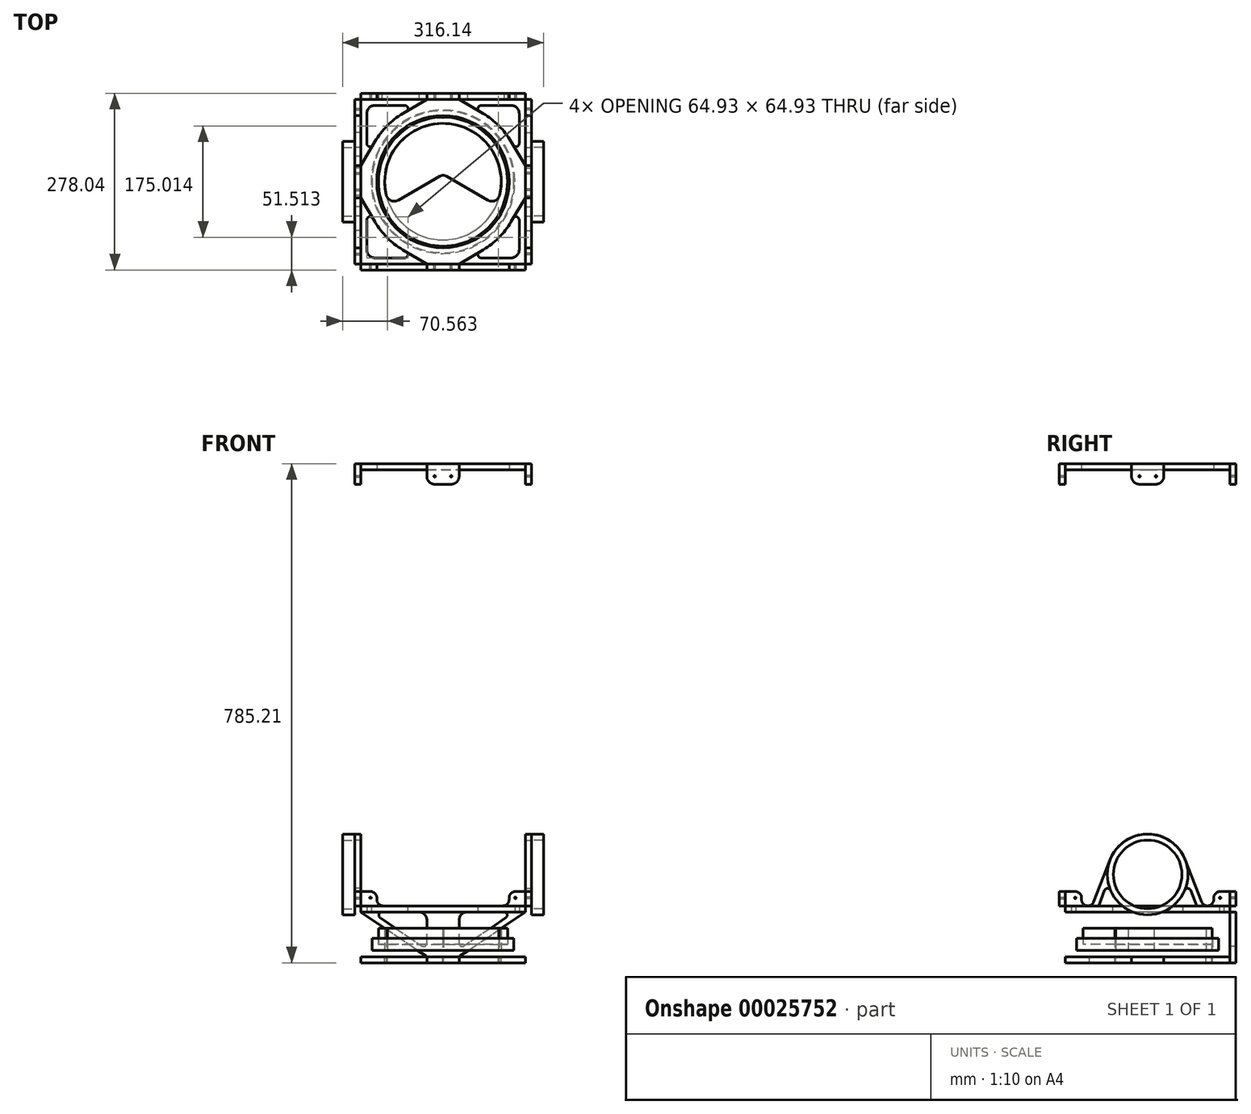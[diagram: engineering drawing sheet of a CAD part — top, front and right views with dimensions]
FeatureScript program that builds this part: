
annotation { "Feature Type Name" : "Feature", "Feature Type Description" : "" }
export const myFeature = defineFeature(function(context is Context, id is Id, definition is map)
    precondition{}
    {
        {
            var Q0;
            Q0=qCreatedBy(makeId("Top.planeOp"),FACE);
            var sketch = newSketch(context, id + "F0", { "sketchPlane" : qUnion([Q0])});
            skCircle(sketch, "E0", {"center": v(0, 0) * mm, "radius": 101.6 * mm});
            skCircle(sketch, "E1", {"center": v(0, 0) * mm, "radius": 101.7 * mm});
            skCircle(sketch, "E2", {"center": v(0, 0) * mm, "radius": 111.7 * mm});
            skCircle(sketch, "E3", {"center": v(0, 0) * mm, "radius": 91.7 * mm});
            skCircle(sketch, "E4", {"center": v(0, 0) * mm, "radius": 10 * mm});
            skLineSegment(sketch, "E5", {"start": v(-10, 0) * mm, "end": v(-10, 91.15) * mm});
            skLineSegment(sketch, "E6", {"start": v(10, 0) * mm, "end": v(10, 91.15) * mm});
            skLineSegment(sketch, "E7", {"start": v(-5, -8.66) * mm, "end": v(73.94, -54.24) * mm});
            skLineSegment(sketch, "E8", {"start": v(5, -8.66) * mm, "end": v(-73.94, -54.24) * mm});
            skLineSegment(sketch, "E9", {"start": v(-5, 8.66) * mm, "end": v(-83.94, -36.92) * mm});
            skLineSegment(sketch, "E10", {"start": v(5, 8.66) * mm, "end": v(83.94, -36.92) * mm});
            skSolve(sketch);
        }
        {
            var Q0;
            Q0=makeQuery(id+"F0.imprint","IMPRINT",FACE,{"disambiguationData":[TD([[makeQuery(id+"F0.imprint","IMPRINT",EDGE,{"derivedFrom":sQuery(id+"F0.wireOp",EDGE,"E0")}),1.0]])]});
            var Q1;
            {var subQ1=sQuery(id+"F0.wireOp",EDGE,"E5");var subQ3=sQuery(id+"F0.wireOp",EDGE,"E3");var subQ5=makeQuery(id+"F0.imprint","INTERSECT",VERTEX,{"derivedFrom":[subQ3,subQ1]});Q1=makeQuery(id+"F0.imprint","IMPRINT",FACE,{"disambiguationData":[TD([[makeQuery(id+"F0.imprint","IMPRINT",EDGE,{"disambiguationData":[TD([[subQ5,-1.0]])],"derivedFrom":subQ3}),1.0]])]});}
            var Q2;
            {var subQ1=sQuery(id+"F0.wireOp",EDGE,"E7");var subQ3=sQuery(id+"F0.wireOp",EDGE,"E3");var subQ5=makeQuery(id+"F0.imprint","INTERSECT",VERTEX,{"derivedFrom":[subQ3,subQ1]});Q2=makeQuery(id+"F0.imprint","IMPRINT",FACE,{"disambiguationData":[TD([[makeQuery(id+"F0.imprint","IMPRINT",EDGE,{"disambiguationData":[TD([[subQ5,1.0]])],"derivedFrom":subQ3}),1.0]])]});}
            var Q3;
            {var subQ3=sQuery(id+"F0.wireOp",EDGE,"E3");var subQ5=sQuery(id+"F0.wireOp",EDGE,"E8");var subQ8=makeQuery(id+"F0.imprint","INTERSECT",VERTEX,{"derivedFrom":[subQ3,subQ5]});Q3=makeQuery(id+"F0.imprint","IMPRINT",FACE,{"disambiguationData":[TD([[makeQuery(id+"F0.imprint","IMPRINT",EDGE,{"disambiguationData":[TD([[subQ8,1.0]])],"derivedFrom":subQ3}),1.0]])]});}
            var Q4;
            {var subQ0=sQuery(id+"F0.wireOp",EDGE,"E4");var subQ2=makeQuery(id+"F0.imprint","INTERSECT",VERTEX,{"derivedFrom":[subQ0,sQuery(id+"F0.wireOp",EDGE,"E6")]});Q4=makeQuery(id+"F0.imprint","IMPRINT",FACE,{"disambiguationData":[TD([[makeQuery(id+"F0.imprint","IMPRINT",EDGE,{"disambiguationData":[TD([[subQ2,-1.0]])],"derivedFrom":subQ0}),1.0]])]});}
            var Q5;
            {var subQ1=sQuery(id+"F0.wireOp",EDGE,"E5");var subQ3=sQuery(id+"F0.wireOp",EDGE,"E4");var subQ5=makeQuery(id+"F0.imprint","INTERSECT",VERTEX,{"derivedFrom":[subQ3,subQ1]});Q5=makeQuery(id+"F0.imprint","IMPRINT",FACE,{"disambiguationData":[TD([[makeQuery(id+"F0.imprint","IMPRINT",EDGE,{"disambiguationData":[TD([[subQ5,1.0]])],"derivedFrom":subQ3}),-1.0]])]});}
            var Q6;
            {var subQ0=sQuery(id+"F0.wireOp",EDGE,"E6");var subQ3=sQuery(id+"F0.wireOp",EDGE,"E4");var subQ4=makeQuery(id+"F0.imprint","INTERSECT",VERTEX,{"derivedFrom":[subQ3,subQ0]});Q6=makeQuery(id+"F0.imprint","IMPRINT",FACE,{"disambiguationData":[TD([[makeQuery(id+"F0.imprint","IMPRINT",EDGE,{"disambiguationData":[TD([[subQ4,-1.0]])],"derivedFrom":subQ3}),-1.0]])]});}
            var Q7;
            {var subQ1=sQuery(id+"F0.wireOp",EDGE,"E7");var subQ3=sQuery(id+"F0.wireOp",EDGE,"E4");var subQ5=makeQuery(id+"F0.imprint","INTERSECT",VERTEX,{"derivedFrom":[subQ3,subQ1]});Q7=makeQuery(id+"F0.imprint","IMPRINT",FACE,{"disambiguationData":[TD([[makeQuery(id+"F0.imprint","IMPRINT",EDGE,{"disambiguationData":[TD([[subQ5,-1.0]])],"derivedFrom":subQ3}),-1.0]])]});}
            var Q8;
            {var subQ3=sQuery(id+"F0.wireOp",EDGE,"E3");var subQ6=sQuery(id+"F0.wireOp",EDGE,"E7");var subQ10=makeQuery(id+"F0.imprint","INTERSECT",VERTEX,{"derivedFrom":[subQ3,subQ6]});Q8=makeQuery(id+"F0.imprint","IMPRINT",FACE,{"disambiguationData":[TD([[makeQuery(id+"F0.imprint","IMPRINT",EDGE,{"disambiguationData":[TD([[subQ10,-1.0]])],"derivedFrom":subQ3}),1.0]])]});}
            var Q9;
            {var subQ0=sQuery(id+"F0.wireOp",EDGE,"E6");var subQ3=sQuery(id+"F0.wireOp",EDGE,"E3");var subQ4=makeQuery(id+"F0.imprint","INTERSECT",VERTEX,{"derivedFrom":[subQ3,subQ0]});Q9=makeQuery(id+"F0.imprint","IMPRINT",FACE,{"disambiguationData":[TD([[makeQuery(id+"F0.imprint","IMPRINT",EDGE,{"disambiguationData":[TD([[subQ4,1.0]])],"derivedFrom":subQ3}),1.0]])]});}
            var Q10;
            {var subQ1=sQuery(id+"F0.wireOp",EDGE,"E5");var subQ5=sQuery(id+"F0.wireOp",EDGE,"E3");var subQ6=makeQuery(id+"F0.imprint","INTERSECT",VERTEX,{"derivedFrom":[subQ5,subQ1]});Q10=makeQuery(id+"F0.imprint","IMPRINT",FACE,{"disambiguationData":[TD([[makeQuery(id+"F0.imprint","IMPRINT",EDGE,{"disambiguationData":[TD([[subQ6,1.0]])],"derivedFrom":subQ5}),1.0]])]});}
            extrude(context, id + "F1", {"entities" : qUnion([Q0, Q1, Q2, Q3, Q4, Q5, Q6, Q7, Q8, Q9, Q10]), "depth" : 25.4 * mm});
        }
        {
            var Q0;
            Q0=makeQuery(id+"F0.imprint","IMPRINT",FACE,{"disambiguationData":[TD([[makeQuery(id+"F0.imprint","IMPRINT",EDGE,{"derivedFrom":sQuery(id+"F0.wireOp",EDGE,"E1")}),-1.0]])]});
            extrude(context, id + "F2", {"entities" : qUnion([Q0]), "depth" : 9.52 * mm});
        }
        {
            var Q0;
            Q0=makeQuery(id+"F0.imprint","IMPRINT",FACE,{"disambiguationData":[TD([[makeQuery(id+"F0.imprint","IMPRINT",EDGE,{"derivedFrom":sQuery(id+"F0.wireOp",EDGE,"E1")}),-1.0]])]});
            var Q1;
            Q1=makeQuery(id+"F0.imprint","IMPRINT",FACE,{"disambiguationData":[TD([[makeQuery(id+"F0.imprint","IMPRINT",EDGE,{"derivedFrom":sQuery(id+"F0.wireOp",EDGE,"E0")}),-1.0]])]});
            var Q2;
            Q2=makeQuery(id+"F0.imprint","IMPRINT",FACE,{"disambiguationData":[TD([[makeQuery(id+"F0.imprint","IMPRINT",EDGE,{"derivedFrom":sQuery(id+"F0.wireOp",EDGE,"E0")}),1.0]])]});
            var Q3;
            {var subQ3=sQuery(id+"F0.wireOp",EDGE,"E3");var subQ6=sQuery(id+"F0.wireOp",EDGE,"E7");var subQ10=makeQuery(id+"F0.imprint","INTERSECT",VERTEX,{"derivedFrom":[subQ3,subQ6]});Q3=makeQuery(id+"F0.imprint","IMPRINT",FACE,{"disambiguationData":[TD([[makeQuery(id+"F0.imprint","IMPRINT",EDGE,{"disambiguationData":[TD([[subQ10,-1.0]])],"derivedFrom":subQ3}),1.0]])]});}
            var Q4;
            {var subQ0=sQuery(id+"F0.wireOp",EDGE,"E4");var subQ2=makeQuery(id+"F0.imprint","INTERSECT",VERTEX,{"derivedFrom":[subQ0,sQuery(id+"F0.wireOp",EDGE,"E6")]});Q4=makeQuery(id+"F0.imprint","IMPRINT",FACE,{"disambiguationData":[TD([[makeQuery(id+"F0.imprint","IMPRINT",EDGE,{"disambiguationData":[TD([[subQ2,-1.0]])],"derivedFrom":subQ0}),1.0]])]});}
            var Q5;
            {var subQ1=sQuery(id+"F0.wireOp",EDGE,"E5");var subQ5=sQuery(id+"F0.wireOp",EDGE,"E3");var subQ6=makeQuery(id+"F0.imprint","INTERSECT",VERTEX,{"derivedFrom":[subQ5,subQ1]});Q5=makeQuery(id+"F0.imprint","IMPRINT",FACE,{"disambiguationData":[TD([[makeQuery(id+"F0.imprint","IMPRINT",EDGE,{"disambiguationData":[TD([[subQ6,1.0]])],"derivedFrom":subQ5}),1.0]])]});}
            var Q6;
            {var subQ3=sQuery(id+"F0.wireOp",EDGE,"E3");var subQ5=sQuery(id+"F0.wireOp",EDGE,"E8");var subQ8=makeQuery(id+"F0.imprint","INTERSECT",VERTEX,{"derivedFrom":[subQ3,subQ5]});Q6=makeQuery(id+"F0.imprint","IMPRINT",FACE,{"disambiguationData":[TD([[makeQuery(id+"F0.imprint","IMPRINT",EDGE,{"disambiguationData":[TD([[subQ8,1.0]])],"derivedFrom":subQ3}),1.0]])]});}
            var Q7;
            {var subQ1=sQuery(id+"F0.wireOp",EDGE,"E7");var subQ3=sQuery(id+"F0.wireOp",EDGE,"E4");var subQ5=makeQuery(id+"F0.imprint","INTERSECT",VERTEX,{"derivedFrom":[subQ3,subQ1]});Q7=makeQuery(id+"F0.imprint","IMPRINT",FACE,{"disambiguationData":[TD([[makeQuery(id+"F0.imprint","IMPRINT",EDGE,{"disambiguationData":[TD([[subQ5,-1.0]])],"derivedFrom":subQ3}),-1.0]])]});}
            var Q8;
            {var subQ0=sQuery(id+"F0.wireOp",EDGE,"E6");var subQ3=sQuery(id+"F0.wireOp",EDGE,"E4");var subQ4=makeQuery(id+"F0.imprint","INTERSECT",VERTEX,{"derivedFrom":[subQ3,subQ0]});Q8=makeQuery(id+"F0.imprint","IMPRINT",FACE,{"disambiguationData":[TD([[makeQuery(id+"F0.imprint","IMPRINT",EDGE,{"disambiguationData":[TD([[subQ4,-1.0]])],"derivedFrom":subQ3}),-1.0]])]});}
            var Q9;
            {var subQ1=sQuery(id+"F0.wireOp",EDGE,"E5");var subQ3=sQuery(id+"F0.wireOp",EDGE,"E4");var subQ5=makeQuery(id+"F0.imprint","INTERSECT",VERTEX,{"derivedFrom":[subQ3,subQ1]});Q9=makeQuery(id+"F0.imprint","IMPRINT",FACE,{"disambiguationData":[TD([[makeQuery(id+"F0.imprint","IMPRINT",EDGE,{"disambiguationData":[TD([[subQ5,1.0]])],"derivedFrom":subQ3}),-1.0]])]});}
            extrude(context, id + "F3", {"entities" : qUnion([Q0, Q1, Q2, Q3, Q4, Q5, Q6, Q7, Q8, Q9]), "operationType" : NewBodyOperationType.ADD, "oppositeDirection" : true, "depth" : 9.52 * mm});
        }
        {
            var Q0;
            Q0=makeQuery(id+"F3.opExtrude","SWEPT_EDGE",EDGE,{"disambiguationData":[OSD([sQuery(id+"F0.wireOp",EDGE,"E3"),sQuery(id+"F0.wireOp",EDGE,"E6")])]});
            var Q1;
            Q1=makeQuery(id+"F3.opExtrude","SWEPT_EDGE",EDGE,{"disambiguationData":[OSD([sQuery(id+"F0.wireOp",EDGE,"E7"),sQuery(id+"F0.wireOp",EDGE,"E8")])]});
            var Q2;
            Q2=makeQuery(id+"F3.opExtrude","SWEPT_EDGE",EDGE,{"disambiguationData":[OSD([sQuery(id+"F0.wireOp",EDGE,"E3"),sQuery(id+"F0.wireOp",EDGE,"E5")])]});
            var Q3;
            Q3=makeQuery(id+"F3.opExtrude","SWEPT_EDGE",EDGE,{"disambiguationData":[OSD([sQuery(id+"F0.wireOp",EDGE,"E5"),sQuery(id+"F0.wireOp",EDGE,"E9")])]});
            var Q4;
            Q4=makeQuery(id+"F3.opExtrude","SWEPT_EDGE",EDGE,{"disambiguationData":[OSD([sQuery(id+"F0.wireOp",EDGE,"E3"),sQuery(id+"F0.wireOp",EDGE,"E10")])]});
            var Q5;
            Q5=makeQuery(id+"F3.opExtrude","SWEPT_EDGE",EDGE,{"disambiguationData":[OSD([sQuery(id+"F0.wireOp",EDGE,"E3"),sQuery(id+"F0.wireOp",EDGE,"E7")])]});
            var Q6;
            Q6=makeQuery(id+"F3.opExtrude","SWEPT_EDGE",EDGE,{"disambiguationData":[OSD([sQuery(id+"F0.wireOp",EDGE,"E6"),sQuery(id+"F0.wireOp",EDGE,"E10")])]});
            var Q7;
            Q7=makeQuery(id+"F3.opExtrude","SWEPT_EDGE",EDGE,{"disambiguationData":[OSD([sQuery(id+"F0.wireOp",EDGE,"E3"),sQuery(id+"F0.wireOp",EDGE,"E9")])]});
            var Q8;
            Q8=makeQuery(id+"F3.opExtrude","SWEPT_EDGE",EDGE,{"disambiguationData":[OSD([sQuery(id+"F0.wireOp",EDGE,"E3"),sQuery(id+"F0.wireOp",EDGE,"E8")])]});
            fillet(context, id + "F4", {"entities" : qUnion([Q0, Q1, Q2, Q3, Q4, Q5, Q6, Q7, Q8]), "radius" : 12.7 * mm, "tangentPropagation" : true, "allowEdgeOverflow" : false});
        }
        {
            var Q0;
            Q0=makeQuery(id+"F3.opExtrude","CAP_FACE",FACE,{"disambiguationData":[OSD([sQuery(id+"F0.wireOp",EDGE,"E2"),sQuery(id+"F0.wireOp",EDGE,"E3"),sQuery(id+"F0.wireOp",EDGE,"E5"),sQuery(id+"F0.wireOp",EDGE,"E6"),sQuery(id+"F0.wireOp",EDGE,"E7"),sQuery(id+"F0.wireOp",EDGE,"E8"),sQuery(id+"F0.wireOp",EDGE,"E9"),sQuery(id+"F0.wireOp",EDGE,"E10")])],"isStart":false});
            var sketch = newSketch(context, id + "F5", { "sketchPlane" : qUnion([Q0])});
            skCircle(sketch, "E11", {"center": v(-88.08, 50.85) * mm, "radius": 0.64 * mm});
            skCircle(sketch, "E12", {"center": v(0, -101.7) * mm, "radius": 0.64 * mm});
            skCircle(sketch, "E13", {"center": v(88.08, 50.85) * mm, "radius": 0.64 * mm});
            skSolve(sketch);
        }
        {
            var Q0;
            Q0 = qSketchRegion(id + "F5", true);
            extrude(context, id + "F6", {"entities" : qUnion([Q0]), "operationType" : NewBodyOperationType.REMOVE, "endBound" : BoundingType.UP_TO_NEXT, "oppositeDirection" : true, "depth" : 25.4 * mm});
        }
        {
            var Q0;
            Q0=qCreatedBy(makeId("Front.planeOp"),FACE);
            var sketch = newSketch(context, id + "F7", { "sketchPlane" : qUnion([Q0])});
            skLineSegment(sketch, "E14", {"start": v(0, 0) * mm, "end": v(0, -19.69) * mm});
            skLineSegment(sketch, "E15", {"start": v(0, -19.69) * mm, "end": v(111.54, -19.69) * mm});
            skLineSegment(sketch, "E16", {"start": v(0, 0) * mm, "end": v(0, 50.8) * mm});
            skLineSegment(sketch, "E17", {"start": v(0, 50.8) * mm, "end": v(25.02, 50.8) * mm});
            skLineSegment(sketch, "E18", {"start": v(0, 25.4) * mm, "end": v(0, 880.87) * mm});
            skLineSegment(sketch, "E19", {"start": v(0, 746.48) * mm, "end": v(20.65, 746.48) * mm});
            skSolve(sketch);
        }
        {
            var Q0;
            Q0 = qSketchRegion(id + "F7", true);
            var Q1;
            Q1=sQuery(id+"F7.wireOp",EDGE,"E15");
            var Q2;
            Q2=sQuery(id+"F7.wireOp",EDGE,"E14");
            revolve(context, id + "F8", {"bodyType" : ExtendedToolBodyType.SURFACE, "entities" : qUnion([Q0]), "surfaceEntities" : qUnion([Q1]), "axis" : qUnion([Q2]), "revolveType" : RevolveType.FULL});
        }
        {
            var Q0;
            Q0=makeQuery(id+"F8.opRevolve","SWEPT_FACE",FACE,{"disambiguationData":[OSD([sQuery(id+"F7.wireOp",EDGE,"E15")])]});
            var sketch = newSketch(context, id + "F9", { "sketchPlane" : qUnion([Q0])});
            skLineSegment(sketch, "E20", {"start": v(129.16, 0) * mm, "end": v(-129.5, 0) * mm, "construction": true});
            skLineSegment(sketch, "E21", {"start": v(-129.5, 25.4) * mm, "end": v(-129.5, -25.4) * mm});
            skPoint(sketch, "E22", {"position": v(-129.5, 0) * mm});
            skLineSegment(sketch, "E23", {"start": v(0, 0) * mm, "end": v(0, 124.42) * mm, "construction": true});
            skLineSegment(sketch, "E24", {"start": v(-129.5, 25.4) * mm, "end": v(-107.12, 63.28) * mm});
            skLineSegment(sketch, "E25.MirrorCS", {"start": v(129.5, 25.4) * mm, "end": v(129.5, -25.4) * mm});
            skLineSegment(sketch, "E26.MirrorCS", {"start": v(129.5, 25.4) * mm, "end": v(107.12, 63.28) * mm});
            skLineSegment(sketch, "E27.MirrorCS", {"start": v(-129.5, -25.4) * mm, "end": v(-107.12, -63.28) * mm});
            skLineSegment(sketch, "E28.MirrorCS", {"start": v(129.5, -25.4) * mm, "end": v(107.12, -63.28) * mm});
            skCircle(sketch, "E29", {"center": v(0, 0) * mm, "radius": 91.7 * mm});
            skCircle(sketch, "E30", {"center": v(88.08, 50.85) * mm, "radius": 0.64 * mm});
            skCircle(sketch, "E31", {"center": v(-88.08, 50.85) * mm, "radius": 0.64 * mm});
            skCircle(sketch, "E32", {"center": v(0, -101.7) * mm, "radius": 0.64 * mm});
            skLineSegment(sketch, "E33.1.0", {"start": v(-25.4, 129.5) * mm, "end": v(-63.28, 107.12) * mm});
            skLineSegment(sketch, "E33.1.1", {"start": v(25.4, 129.5) * mm, "end": v(-25.4, 129.5) * mm});
            skLineSegment(sketch, "E33.1.2", {"start": v(25.4, 129.5) * mm, "end": v(63.28, 107.12) * mm});
            skLineSegment(sketch, "E33.1.3", {"start": v(25.4, -129.5) * mm, "end": v(63.28, -107.12) * mm});
            skLineSegment(sketch, "E33.1.4", {"start": v(25.4, -129.5) * mm, "end": v(-25.4, -129.5) * mm});
            skLineSegment(sketch, "E33.1.5", {"start": v(-25.4, -129.5) * mm, "end": v(-63.28, -107.12) * mm});
            skLineSegment(sketch, "E33.anchor1", {"start": v(0, 0) * mm, "end": v(-107.12, -63.28) * mm, "construction": true});
            skLineSegment(sketch, "E33.anchor2", {"start": v(0, 0) * mm, "end": v(-63.28, 107.12) * mm, "construction": true});
            skArc(sketch, "E34", {"start": v(-107.12, -63.28) * mm, "mid": v(-87.98, -87.98) * mm, "end": v(-63.28, -107.12) * mm});
            skArc(sketch, "E35", {"start": v(63.28, -107.12) * mm, "mid": v(87.98, -87.98) * mm, "end": v(107.12, -63.28) * mm});
            skArc(sketch, "E36", {"start": v(107.12, 63.28) * mm, "mid": v(87.98, 87.98) * mm, "end": v(63.28, 107.12) * mm});
            skArc(sketch, "E37", {"start": v(-63.28, 107.12) * mm, "mid": v(-87.98, 87.98) * mm, "end": v(-107.12, 63.28) * mm});
            skLineSegment(sketch, "E38", {"start": v(-129.5, -25.4) * mm, "end": v(-119.97, -25.4) * mm});
            skLineSegment(sketch, "E39", {"start": v(-119.97, -25.4) * mm, "end": v(-119.97, 25.4) * mm});
            skLineSegment(sketch, "E40", {"start": v(-119.97, 25.4) * mm, "end": v(-129.5, 25.4) * mm});
            skLineSegment(sketch, "E41", {"start": v(-25.4, -129.5) * mm, "end": v(-25.4, -119.97) * mm});
            skLineSegment(sketch, "E42", {"start": v(-25.4, -119.97) * mm, "end": v(25.4, -119.97) * mm});
            skLineSegment(sketch, "E43", {"start": v(25.4, -119.97) * mm, "end": v(25.4, -129.5) * mm});
            skLineSegment(sketch, "E44", {"start": v(129.5, -25.4) * mm, "end": v(119.97, -25.4) * mm});
            skLineSegment(sketch, "E45", {"start": v(119.97, -25.4) * mm, "end": v(119.97, 25.4) * mm});
            skLineSegment(sketch, "E46", {"start": v(119.97, 25.4) * mm, "end": v(129.5, 25.4) * mm});
            skLineSegment(sketch, "E47", {"start": v(-25.4, 129.5) * mm, "end": v(-25.4, 119.97) * mm});
            skLineSegment(sketch, "E48", {"start": v(-25.4, 119.97) * mm, "end": v(25.4, 119.97) * mm});
            skLineSegment(sketch, "E49", {"start": v(25.4, 119.97) * mm, "end": v(25.4, 129.5) * mm});
            skSolve(sketch);
        }
        {
            var Q0;
            Q0 = qSketchRegion(id + "F9", true);
            extrude(context, id + "F10", {"entities" : qUnion([Q0]), "depth" : 9.52 * mm});
        }
        {
            var Q0;
            Q0=sQuery(id+"F7.wireOp",EDGE,"E17");
            var Q1;
            Q1=sQuery(id+"F7.wireOp",EDGE,"E16");
            revolve(context, id + "F11", {"bodyType" : ExtendedToolBodyType.SURFACE, "surfaceEntities" : qUnion([Q0]), "axis" : qUnion([Q1]), "revolveType" : RevolveType.FULL});
        }
        {
            var Q0;
            Q0=makeQuery(id+"F11.opRevolve","SWEPT_FACE",FACE,{"disambiguationData":[OSD([sQuery(id+"F7.wireOp",EDGE,"E17")])]});
            var sketch = newSketch(context, id + "F12", { "sketchPlane" : qUnion([Q0])});
            skCircle(sketch, "E50", {"center": v(0, 0) * mm, "radius": 113.03 * mm});
            skLineSegment(sketch, "E51.rect.bottom", {"start": v(129.5, 129.5) * mm, "end": v(-129.5, 129.5) * mm});
            skLineSegment(sketch, "E51.rect.top", {"start": v(129.5, -129.5) * mm, "end": v(-129.5, -129.5) * mm});
            skLineSegment(sketch, "E51.rect.left", {"start": v(129.5, 129.5) * mm, "end": v(129.5, -129.5) * mm});
            skLineSegment(sketch, "E51.rect.right", {"start": v(-129.5, 129.5) * mm, "end": v(-129.5, -129.5) * mm});
            skLineSegment(sketch, "E52.rect.bottom", {"start": v(107.27, 119.97) * mm, "end": v(-107.27, 119.97) * mm});
            skLineSegment(sketch, "E52.rect.top", {"start": v(107.27, -119.97) * mm, "end": v(-107.27, -119.97) * mm});
            skLineSegment(sketch, "E52.rect.left", {"start": v(119.97, 107.27) * mm, "end": v(119.97, -107.27) * mm});
            skLineSegment(sketch, "E52.rect.right", {"start": v(-119.97, 107.27) * mm, "end": v(-119.97, -107.27) * mm});
            skPoint(sketch, "E53.visualSharp", {"position": v(-119.97, 119.97) * mm});
            skArc(sketch, "E53.filletArc", {"start": v(-107.27, 119.97) * mm, "mid": v(-116.25, 116.25) * mm, "end": v(-119.97, 107.27) * mm});
            skPoint(sketch, "E54.visualSharp", {"position": v(119.97, 119.97) * mm});
            skArc(sketch, "E54.filletArc", {"start": v(119.97, 107.27) * mm, "mid": v(116.25, 116.25) * mm, "end": v(107.27, 119.97) * mm});
            skPoint(sketch, "E55.visualSharp", {"position": v(-119.97, -119.97) * mm});
            skArc(sketch, "E55.filletArc", {"start": v(-119.97, -107.27) * mm, "mid": v(-116.25, -116.25) * mm, "end": v(-107.27, -119.97) * mm});
            skPoint(sketch, "E56.visualSharp", {"position": v(119.97, -119.97) * mm});
            skArc(sketch, "E56.filletArc", {"start": v(107.27, -119.97) * mm, "mid": v(116.25, -116.25) * mm, "end": v(119.97, -107.27) * mm});
            skArc(sketch, "E57", {"start": v(-63.28, 107.12) * mm, "mid": v(-87.98, 87.98) * mm, "end": v(-107.12, 63.28) * mm});
            skLineSegment(sketch, "E58", {"start": v(-63.28, 107.12) * mm, "end": v(-41.53, 119.97) * mm});
            skLineSegment(sketch, "E59", {"start": v(-107.12, 63.28) * mm, "end": v(-119.97, 41.53) * mm});
            skArc(sketch, "E60.MirrorCS", {"start": v(63.28, 107.12) * mm, "mid": v(87.98, 87.98) * mm, "end": v(107.12, 63.28) * mm});
            skLineSegment(sketch, "E61.MirrorCS", {"start": v(63.28, 107.12) * mm, "end": v(41.53, 119.97) * mm});
            skLineSegment(sketch, "E62.MirrorCS", {"start": v(107.12, 63.28) * mm, "end": v(119.97, 41.53) * mm});
            skArc(sketch, "E63.MirrorCS", {"start": v(-63.28, -107.12) * mm, "mid": v(-87.98, -87.98) * mm, "end": v(-107.12, -63.28) * mm});
            skLineSegment(sketch, "E64.MirrorCS", {"start": v(-107.12, -63.28) * mm, "end": v(-119.97, -41.53) * mm});
            skLineSegment(sketch, "E65.MirrorCS", {"start": v(63.28, -107.12) * mm, "end": v(41.53, -119.97) * mm});
            skArc(sketch, "E66.MirrorCS", {"start": v(63.28, -107.12) * mm, "mid": v(87.98, -87.98) * mm, "end": v(107.12, -63.28) * mm});
            skLineSegment(sketch, "E67.MirrorCS", {"start": v(107.12, -63.28) * mm, "end": v(119.97, -41.53) * mm});
            skLineSegment(sketch, "E68.MirrorCS", {"start": v(-63.28, -107.12) * mm, "end": v(-41.53, -119.97) * mm});
            skSolve(sketch);
        }
        {
            var Q0;
            Q0=makeQuery(id+"F12.imprint","IMPRINT",FACE,{"disambiguationData":[TD([[makeQuery(id+"F12.imprint","IMPRINT",EDGE,{"derivedFrom":sQuery(id+"F12.wireOp",EDGE,"E51.rect.bottom")}),1.0]])]});
            var Q1;
            Q1=makeQuery(id+"F12.imprint","IMPRINT",FACE,{"disambiguationData":[TD([[makeQuery(id+"F12.imprint","IMPRINT",EDGE,{"derivedFrom":sQuery(id+"F12.wireOp",EDGE,"E50")}),-1.0]])]});
            extrude(context, id + "F13", {"entities" : qUnion([Q0, Q1]), "depth" : 9.52 * mm});
        }
        {
            var Q0;
            Q0=makeQuery(id+"F13.opExtrude","SWEPT_EDGE",EDGE,{"disambiguationData":[OSD([sQuery(id+"F12.wireOp",EDGE,"E52.rect.bottom"),sQuery(id+"F12.wireOp",EDGE,"E58")])]});
            var Q1;
            Q1=makeQuery(id+"F13.opExtrude","SWEPT_EDGE",EDGE,{"disambiguationData":[OSD([sQuery(id+"F12.wireOp",EDGE,"E52.rect.right"),sQuery(id+"F12.wireOp",EDGE,"E59")])]});
            var Q2;
            Q2=makeQuery(id+"F13.opExtrude","SWEPT_EDGE",EDGE,{"disambiguationData":[OSD([sQuery(id+"F12.wireOp",EDGE,"E52.rect.bottom"),sQuery(id+"F12.wireOp",EDGE,"E61.MirrorCS")])]});
            var Q3;
            Q3=makeQuery(id+"F13.opExtrude","SWEPT_EDGE",EDGE,{"disambiguationData":[OSD([sQuery(id+"F12.wireOp",EDGE,"E52.rect.left"),sQuery(id+"F12.wireOp",EDGE,"E62.MirrorCS")])]});
            var Q4;
            Q4=makeQuery(id+"F13.opExtrude","SWEPT_EDGE",EDGE,{"disambiguationData":[OSD([sQuery(id+"F12.wireOp",EDGE,"E52.rect.left"),sQuery(id+"F12.wireOp",EDGE,"E67.MirrorCS")])]});
            var Q5;
            Q5=makeQuery(id+"F13.opExtrude","SWEPT_EDGE",EDGE,{"disambiguationData":[OSD([sQuery(id+"F12.wireOp",EDGE,"E52.rect.right"),sQuery(id+"F12.wireOp",EDGE,"E64.MirrorCS")])]});
            var Q6;
            Q6=makeQuery(id+"F13.opExtrude","SWEPT_EDGE",EDGE,{"disambiguationData":[OSD([sQuery(id+"F12.wireOp",EDGE,"E52.rect.top"),sQuery(id+"F12.wireOp",EDGE,"E68.MirrorCS")])]});
            var Q7;
            Q7=makeQuery(id+"F13.opExtrude","SWEPT_EDGE",EDGE,{"disambiguationData":[OSD([sQuery(id+"F12.wireOp",EDGE,"E52.rect.top"),sQuery(id+"F12.wireOp",EDGE,"E65.MirrorCS")])]});
            fillet(context, id + "F14", {"entities" : qUnion([Q0, Q1, Q2, Q3, Q4, Q5, Q6, Q7]), "radius" : 5.08 * mm, "tangentPropagation" : true, "allowEdgeOverflow" : false});
        }
        {
            var Q0;
            Q0=makeQuery(id+"F13.opExtrude","SWEPT_FACE",FACE,{"disambiguationData":[OSD([sQuery(id+"F12.wireOp",EDGE,"E51.rect.bottom")])]});
            var sketch = newSketch(context, id + "F15", { "sketchPlane" : qUnion([Q0])});
            skLineSegment(sketch, "E69", {"start": v(-25.4, -29.21) * mm, "end": v(-25.4, -21.03) * mm});
            skLineSegment(sketch, "E70", {"start": v(-26.52, -18.93) * mm, "end": v(-128.38, 50.04) * mm});
            skLineSegment(sketch, "E71", {"start": v(-25.4, -29.21) * mm, "end": v(25.4, -29.21) * mm});
            skLineSegment(sketch, "E72", {"start": v(25.4, -29.21) * mm, "end": v(25.4, -21.03) * mm});
            skLineSegment(sketch, "E73", {"start": v(26.52, -18.93) * mm, "end": v(128.38, 50.04) * mm});
            skLineSegment(sketch, "E74", {"start": v(-129.5, 52.15) * mm, "end": v(-129.5, 82.93) * mm});
            skLineSegment(sketch, "E75", {"start": v(-129.5, 82.93) * mm, "end": v(-114, 82.93) * mm});
            skLineSegment(sketch, "E76", {"start": v(-104.1, 73.03) * mm, "end": v(-104.1, 70.23) * mm});
            skLineSegment(sketch, "E77.MirrorCS", {"start": v(129.5, 82.93) * mm, "end": v(114, 82.93) * mm});
            skLineSegment(sketch, "E78.MirrorCS", {"start": v(129.5, 52.15) * mm, "end": v(129.5, 82.93) * mm});
            skLineSegment(sketch, "E79.MirrorCS", {"start": v(104.1, 73.03) * mm, "end": v(104.1, 70.23) * mm});
            skLineSegment(sketch, "E80", {"start": v(-94.2, 60.33) * mm, "end": v(94.2, 60.33) * mm});
            skPoint(sketch, "E81.visualSharp", {"position": v(-104.1, 82.93) * mm});
            skArc(sketch, "E81.filletArc", {"start": v(-104.1, 73.03) * mm, "mid": v(-107, 80.03) * mm, "end": v(-114, 82.93) * mm});
            skPoint(sketch, "E82.visualSharp", {"position": v(104.1, 82.93) * mm});
            skArc(sketch, "E82.filletArc", {"start": v(114, 82.93) * mm, "mid": v(107, 80.03) * mm, "end": v(104.1, 73.03) * mm});
            skPoint(sketch, "E83.visualSharp", {"position": v(104.1, 60.33) * mm});
            skArc(sketch, "E83.filletArc", {"start": v(94.2, 60.33) * mm, "mid": v(101.2, 63.23) * mm, "end": v(104.1, 70.23) * mm});
            skPoint(sketch, "E84.visualSharp", {"position": v(-104.1, 60.33) * mm});
            skArc(sketch, "E84.filletArc", {"start": v(-104.1, 70.23) * mm, "mid": v(-101.2, 63.23) * mm, "end": v(-94.2, 60.33) * mm});
            skPoint(sketch, "E85.visualSharp", {"position": v(-129.5, 50.8) * mm});
            skArc(sketch, "E85.filletArc", {"start": v(-129.5, 52.15) * mm, "mid": v(-129.2, 50.96) * mm, "end": v(-128.38, 50.04) * mm});
            skPoint(sketch, "E86.visualSharp", {"position": v(129.5, 50.8) * mm});
            skArc(sketch, "E86.filletArc", {"start": v(128.38, 50.04) * mm, "mid": v(129.2, 50.96) * mm, "end": v(129.5, 52.15) * mm});
            skPoint(sketch, "E87.visualSharp", {"position": v(-25.4, -19.69) * mm});
            skArc(sketch, "E87.filletArc", {"start": v(-25.4, -21.03) * mm, "mid": v(-25.7, -19.84) * mm, "end": v(-26.52, -18.93) * mm});
            skPoint(sketch, "E88.visualSharp", {"position": v(25.4, -19.69) * mm});
            skArc(sketch, "E88.filletArc", {"start": v(26.52, -18.93) * mm, "mid": v(25.7, -19.84) * mm, "end": v(25.4, -21.03) * mm});
            skLineSegment(sketch, "E89", {"start": v(-25.4, 1.4) * mm, "end": v(-25.4, 38.1) * mm});
            skLineSegment(sketch, "E90", {"start": v(-38.1, 50.8) * mm, "end": v(-95.95, 50.8) * mm});
            skLineSegment(sketch, "E91", {"start": v(-98.8, 41.51) * mm, "end": v(-33.33, -2.81) * mm});
            skPoint(sketch, "E92.visualSharp", {"position": v(-112.5, 50.8) * mm});
            skArc(sketch, "E92.filletArc", {"start": v(-95.95, 50.8) * mm, "mid": v(-100.8, 47.2) * mm, "end": v(-98.8, 41.51) * mm});
            skPoint(sketch, "E93.visualSharp", {"position": v(-25.4, -8.18) * mm});
            skArc(sketch, "E93.filletArc", {"start": v(-33.33, -2.81) * mm, "mid": v(-28.1, -3.1) * mm, "end": v(-25.4, 1.4) * mm});
            skPoint(sketch, "E94.visualSharp", {"position": v(-25.4, 50.8) * mm});
            skArc(sketch, "E94.filletArc", {"start": v(-25.4, 38.1) * mm, "mid": v(-29.12, 47.08) * mm, "end": v(-38.1, 50.8) * mm});
            skLineSegment(sketch, "E95.MirrorCS", {"start": v(25.4, 1.4) * mm, "end": v(25.4, 38.1) * mm});
            skArc(sketch, "E96.MirrorCS", {"start": v(33.33, -2.81) * mm, "mid": v(28.1, -3.1) * mm, "end": v(25.4, 1.4) * mm});
            skLineSegment(sketch, "E97.MirrorCS", {"start": v(98.8, 41.51) * mm, "end": v(33.33, -2.81) * mm});
            skArc(sketch, "E98.MirrorCS", {"start": v(95.95, 50.8) * mm, "mid": v(100.8, 47.2) * mm, "end": v(98.8, 41.51) * mm});
            skLineSegment(sketch, "E99.MirrorCS", {"start": v(38.1, 50.8) * mm, "end": v(95.95, 50.8) * mm});
            skArc(sketch, "E100.MirrorCS", {"start": v(25.4, 38.1) * mm, "mid": v(29.12, 47.08) * mm, "end": v(38.1, 50.8) * mm});
            skCircle(sketch, "E101", {"center": v(-114, 73.03) * mm, "radius": 1.27 * mm});
            skCircle(sketch, "E102", {"center": v(114, 73.03) * mm, "radius": 1.27 * mm});
            skSolve(sketch);
        }
        {
            var Q0;
            {var subQ2=sQuery(id+"F15.wireOp",EDGE,"E75");Q0=makeQuery(id+"F15.imprint","IMPRINT",FACE,{"disambiguationData":[TD([[makeQuery(id+"F15.imprint","IMPRINT",EDGE,{"derivedFrom":subQ2}),-1.0]])]});}
            var Q1;
            {var subQ2=sQuery(id+"F15.wireOp",EDGE,"E80");Q1=makeQuery(id+"F15.imprint","IMPRINT",FACE,{"disambiguationData":[TD([[makeQuery(id+"F15.imprint","IMPRINT",EDGE,{"derivedFrom":subQ2}),-1.0]])]});}
            var Q2;
            Q2=makeQuery(id+"F15.imprint","IMPRINT",FACE,{"disambiguationData":[TD([[makeQuery(id+"F15.imprint","IMPRINT",EDGE,{"derivedFrom":sQuery(id+"F15.wireOp",EDGE,"E69")}),-1.0]])]});
            var Q3;
            {var subQ4=sQuery(id+"F15.wireOp",EDGE,"E77.MirrorCS");Q3=makeQuery(id+"F15.imprint","IMPRINT",FACE,{"disambiguationData":[TD([[makeQuery(id+"F15.imprint","IMPRINT",EDGE,{"derivedFrom":subQ4}),1.0]])]});}
            extrude(context, id + "F16", {"entities" : qUnion([Q0, Q1, Q2, Q3]), "depth" : 9.52 * mm});
        }
        {
            var Q0;
            Q0=makeQuery(id+"F16.opExtrude","SWEPT_BODY",BODY,{"disambiguationData":[OSD([sQuery(id+"F15.wireOp",EDGE,"E69"),sQuery(id+"F15.wireOp",EDGE,"E70"),sQuery(id+"F15.wireOp",EDGE,"E71"),sQuery(id+"F15.wireOp",EDGE,"E72"),sQuery(id+"F15.wireOp",EDGE,"E73"),sQuery(id+"F15.wireOp",EDGE,"E74"),sQuery(id+"F15.wireOp",EDGE,"E75"),sQuery(id+"F15.wireOp",EDGE,"E76"),sQuery(id+"F15.wireOp",EDGE,"E77.MirrorCS"),sQuery(id+"F15.wireOp",EDGE,"E78.MirrorCS"),sQuery(id+"F15.wireOp",EDGE,"E79.MirrorCS"),sQuery(id+"F15.wireOp",EDGE,"E80"),sQuery(id+"F15.wireOp",EDGE,"E81.filletArc"),sQuery(id+"F15.wireOp",EDGE,"E82.filletArc"),sQuery(id+"F15.wireOp",EDGE,"E83.filletArc"),sQuery(id+"F15.wireOp",EDGE,"E84.filletArc"),sQuery(id+"F15.wireOp",EDGE,"E85.filletArc"),sQuery(id+"F15.wireOp",EDGE,"E86.filletArc"),sQuery(id+"F15.wireOp",EDGE,"E87.filletArc"),sQuery(id+"F15.wireOp",EDGE,"E88.filletArc"),sQuery(id+"F15.wireOp",EDGE,"E89"),sQuery(id+"F15.wireOp",EDGE,"E90"),sQuery(id+"F15.wireOp",EDGE,"E91"),sQuery(id+"F15.wireOp",EDGE,"E92.filletArc"),sQuery(id+"F15.wireOp",EDGE,"E93.filletArc"),sQuery(id+"F15.wireOp",EDGE,"E94.filletArc"),sQuery(id+"F15.wireOp",EDGE,"E95.MirrorCS"),sQuery(id+"F15.wireOp",EDGE,"E96.MirrorCS"),sQuery(id+"F15.wireOp",EDGE,"E97.MirrorCS"),sQuery(id+"F15.wireOp",EDGE,"E98.MirrorCS"),sQuery(id+"F15.wireOp",EDGE,"E99.MirrorCS"),sQuery(id+"F15.wireOp",EDGE,"E100.MirrorCS"),sQuery(id+"F15.wireOp",EDGE,"E101"),sQuery(id+"F15.wireOp",EDGE,"E102")])]});
            var Q1;
            Q1=qCreatedBy(makeId("Front.planeOp"),FACE);
            mirror(context, id + "F17", {"entities" : qUnion([Q0]), "mirrorPlane" : qUnion([Q1])});
        }
        {
            var Q0;
            Q0=makeQuery(id+"F17.opPattern","COPY",BODY,{"derivedFrom":makeQuery(id+"F16.opExtrude","SWEPT_BODY",BODY,{"disambiguationData":[OSD([sQuery(id+"F15.wireOp",EDGE,"E69"),sQuery(id+"F15.wireOp",EDGE,"E70"),sQuery(id+"F15.wireOp",EDGE,"E71"),sQuery(id+"F15.wireOp",EDGE,"E72"),sQuery(id+"F15.wireOp",EDGE,"E73"),sQuery(id+"F15.wireOp",EDGE,"E74"),sQuery(id+"F15.wireOp",EDGE,"E75"),sQuery(id+"F15.wireOp",EDGE,"E76"),sQuery(id+"F15.wireOp",EDGE,"E77.MirrorCS"),sQuery(id+"F15.wireOp",EDGE,"E78.MirrorCS"),sQuery(id+"F15.wireOp",EDGE,"E79.MirrorCS"),sQuery(id+"F15.wireOp",EDGE,"E80"),sQuery(id+"F15.wireOp",EDGE,"E81.filletArc"),sQuery(id+"F15.wireOp",EDGE,"E82.filletArc"),sQuery(id+"F15.wireOp",EDGE,"E83.filletArc"),sQuery(id+"F15.wireOp",EDGE,"E84.filletArc"),sQuery(id+"F15.wireOp",EDGE,"E85.filletArc"),sQuery(id+"F15.wireOp",EDGE,"E86.filletArc"),sQuery(id+"F15.wireOp",EDGE,"E87.filletArc"),sQuery(id+"F15.wireOp",EDGE,"E88.filletArc"),sQuery(id+"F15.wireOp",EDGE,"E89"),sQuery(id+"F15.wireOp",EDGE,"E90"),sQuery(id+"F15.wireOp",EDGE,"E91"),sQuery(id+"F15.wireOp",EDGE,"E92.filletArc"),sQuery(id+"F15.wireOp",EDGE,"E93.filletArc"),sQuery(id+"F15.wireOp",EDGE,"E94.filletArc"),sQuery(id+"F15.wireOp",EDGE,"E95.MirrorCS"),sQuery(id+"F15.wireOp",EDGE,"E96.MirrorCS"),sQuery(id+"F15.wireOp",EDGE,"E97.MirrorCS"),sQuery(id+"F15.wireOp",EDGE,"E98.MirrorCS"),sQuery(id+"F15.wireOp",EDGE,"E99.MirrorCS"),sQuery(id+"F15.wireOp",EDGE,"E100.MirrorCS"),sQuery(id+"F15.wireOp",EDGE,"E101"),sQuery(id+"F15.wireOp",EDGE,"E102")])]}),"instanceName":"1"});
            var Q1;
            Q1=sQuery(id+"F7.wireOp",EDGE,"E16");
            transform(context, id + "F18", {"entities" : qUnion([Q0]), "transformType" : TransformType.ROTATION, "transformAxis" : qUnion([Q1]), "angle" : 90 * degree, "makeCopy" : true});
        }
        {
            var Q0;
            Q0=makeQuery(id+"F18.opPattern","COPY",FACE,{"derivedFrom":makeQuery(id+"F17.opPattern","COPY",FACE,{"derivedFrom":makeQuery(id+"F16.opExtrude","CAP_FACE",FACE,{"disambiguationData":[OSD([sQuery(id+"F15.wireOp",EDGE,"E69"),sQuery(id+"F15.wireOp",EDGE,"E70"),sQuery(id+"F15.wireOp",EDGE,"E71"),sQuery(id+"F15.wireOp",EDGE,"E72"),sQuery(id+"F15.wireOp",EDGE,"E73"),sQuery(id+"F15.wireOp",EDGE,"E74"),sQuery(id+"F15.wireOp",EDGE,"E75"),sQuery(id+"F15.wireOp",EDGE,"E76"),sQuery(id+"F15.wireOp",EDGE,"E77.MirrorCS"),sQuery(id+"F15.wireOp",EDGE,"E78.MirrorCS"),sQuery(id+"F15.wireOp",EDGE,"E79.MirrorCS"),sQuery(id+"F15.wireOp",EDGE,"E80"),sQuery(id+"F15.wireOp",EDGE,"E81.filletArc"),sQuery(id+"F15.wireOp",EDGE,"E82.filletArc"),sQuery(id+"F15.wireOp",EDGE,"E83.filletArc"),sQuery(id+"F15.wireOp",EDGE,"E84.filletArc"),sQuery(id+"F15.wireOp",EDGE,"E85.filletArc"),sQuery(id+"F15.wireOp",EDGE,"E86.filletArc"),sQuery(id+"F15.wireOp",EDGE,"E87.filletArc"),sQuery(id+"F15.wireOp",EDGE,"E88.filletArc"),sQuery(id+"F15.wireOp",EDGE,"E89"),sQuery(id+"F15.wireOp",EDGE,"E90"),sQuery(id+"F15.wireOp",EDGE,"E91"),sQuery(id+"F15.wireOp",EDGE,"E92.filletArc"),sQuery(id+"F15.wireOp",EDGE,"E93.filletArc"),sQuery(id+"F15.wireOp",EDGE,"E94.filletArc"),sQuery(id+"F15.wireOp",EDGE,"E95.MirrorCS"),sQuery(id+"F15.wireOp",EDGE,"E96.MirrorCS"),sQuery(id+"F15.wireOp",EDGE,"E97.MirrorCS"),sQuery(id+"F15.wireOp",EDGE,"E98.MirrorCS"),sQuery(id+"F15.wireOp",EDGE,"E99.MirrorCS"),sQuery(id+"F15.wireOp",EDGE,"E100.MirrorCS"),sQuery(id+"F15.wireOp",EDGE,"E101"),sQuery(id+"F15.wireOp",EDGE,"E102")])],"isStart":false}),"instanceName":"1"}),"instanceName":"1"});
            var sketch = newSketch(context, id + "F19", { "sketchPlane" : qUnion([Q0])});
            skPoint(sketch, "E103.startSnap0", {"position": v(0, -29.21) * mm});
            skLineSegment(sketch, "E104", {"start": v(-59.17, 132.86) * mm, "end": v(-84.96, 66.64) * mm});
            skArc(sketch, "E105", {"start": v(-94.2, 60.33) * mm, "mid": v(-88.6, 62.05) * mm, "end": v(-84.96, 66.64) * mm});
            skLineSegment(sketch, "E106.MirrorCS", {"start": v(59.17, 132.86) * mm, "end": v(84.96, 66.64) * mm});
            skArc(sketch, "E107.MirrorCS", {"start": v(94.2, 60.33) * mm, "mid": v(88.6, 62.05) * mm, "end": v(84.96, 66.64) * mm});
            skArc(sketch, "E108", {"start": v(59.17, 132.86) * mm, "mid": v(0, 173.31) * mm, "end": v(-59.17, 132.86) * mm});
            skCircle(sketch, "E109", {"center": v(0, 109.81) * mm, "radius": 53.98 * mm, "construction": true});
            skCircle(sketch, "E110", {"center": v(0, 109.81) * mm, "radius": 53.98 * mm});
            skLineSegment(sketch, "E111", {"start": v(-62.43, 98.23) * mm, "end": v(-77.2, 60.33) * mm});
            skArc(sketch, "E112", {"start": v(-62.43, 98.23) * mm, "mid": v(-54.51, 77.25) * mm, "end": v(-39.79, 60.33) * mm});
            skLineSegment(sketch, "E113", {"start": v(-77.2, 60.33) * mm, "end": v(-39.79, 60.32) * mm});
            skArc(sketch, "E114.MirrorCS", {"start": v(62.43, 98.23) * mm, "mid": v(54.51, 77.25) * mm, "end": v(39.79, 60.33) * mm});
            skLineSegment(sketch, "E115.MirrorCS", {"start": v(62.43, 98.23) * mm, "end": v(77.2, 60.33) * mm});
            skLineSegment(sketch, "E116.MirrorCS", {"start": v(77.2, 60.33) * mm, "end": v(39.79, 60.32) * mm});
            skLineSegment(sketch, "E117", {"start": v(-21.55, 60.33) * mm, "end": v(21.55, 60.33) * mm});
            skSolve(sketch);
        }
        {
            var Q0;
            {var subQ0=sQuery(id+"F19.wireOp",EDGE,"E117");Q0=makeQuery(id+"F19.imprint","IMPRINT",FACE,{"disambiguationData":[TD([[makeQuery(id+"F19.imprint","IMPRINT",EDGE,{"derivedFrom":subQ0}),1.0]])]});}
            var Q1;
            Q1=makeQuery(id+"F19.imprint","IMPRINT",FACE,{"disambiguationData":[TD([[makeQuery(id+"F19.imprint","IMPRINT",EDGE,{"derivedFrom":sQuery(id+"F19.wireOp",EDGE,"E104")}),1.0]])]});
            extrude(context, id + "F20", {"entities" : qUnion([Q0, Q1]), "operationType" : NewBodyOperationType.ADD, "oppositeDirection" : true, "depth" : 9.52 * mm});
        }
        {
            var Q0;
            Q0=makeQuery(id+"F20.opExtrude","SWEPT_EDGE",EDGE,{"disambiguationData":[OSD([sQuery(id+"F19.wireOp",EDGE,"E111"),sQuery(id+"F19.wireOp",EDGE,"E112")])]});
            var Q1;
            Q1=makeQuery(id+"F20.opExtrude","SWEPT_EDGE",EDGE,{"disambiguationData":[OSD([sQuery(id+"F15.wireOp",EDGE,"E80"),sQuery(id+"F19.wireOp",EDGE,"E111"),sQuery(id+"F19.wireOp",EDGE,"E113")])]});
            var Q2;
            Q2=makeQuery(id+"F20.opExtrude","SWEPT_EDGE",EDGE,{"disambiguationData":[OSD([sQuery(id+"F15.wireOp",EDGE,"E80"),sQuery(id+"F19.wireOp",EDGE,"E112"),sQuery(id+"F19.wireOp",EDGE,"E113")])]});
            var Q3;
            {var subQ0=sQuery(id+"F15.wireOp",EDGE,"E80");var subQ1=sQuery(id+"F19.wireOp",EDGE,"E110");var subQ2=sQuery(id+"F19.wireOp",EDGE,"E117");Q3=makeQuery(id+"F20.opExtrude","SWEPT_EDGE",EDGE,{"disambiguationData":[OSD([subQ0,subQ1,subQ2]),TDD([makeQuery(id+"F19.imprint","INTERSECT",VERTEX,{"disambiguationData":[OD(0.0)],"derivedFrom":[makeQuery(id+"F18.opPattern","COPY",EDGE,{"derivedFrom":makeQuery(id+"F17.opPattern","COPY",EDGE,{"derivedFrom":makeQuery(id+"F16.opExtrude","CAP_EDGE",EDGE,{"disambiguationData":[OSD([subQ0])],"isStart":false}),"instanceName":"1"}),"instanceName":"1"}),subQ1,subQ2]})]),ownerDisambiguation([makeQuery(id+"F20.opExtrude","SWEPT_BODY",BODY,{"disambiguationData":[OSD([subQ0,sQuery(id+"F19.wireOp",EDGE,"E104"),sQuery(id+"F19.wireOp",EDGE,"E105"),sQuery(id+"F19.wireOp",EDGE,"E106.MirrorCS"),sQuery(id+"F19.wireOp",EDGE,"E107.MirrorCS"),sQuery(id+"F19.wireOp",EDGE,"E108"),subQ1,sQuery(id+"F19.wireOp",EDGE,"E111"),sQuery(id+"F19.wireOp",EDGE,"E112"),sQuery(id+"F19.wireOp",EDGE,"E114.MirrorCS"),sQuery(id+"F19.wireOp",EDGE,"E115.MirrorCS")])]})])]});}
            var Q4;
            {var subQ0=sQuery(id+"F15.wireOp",EDGE,"E80");var subQ1=sQuery(id+"F19.wireOp",EDGE,"E110");var subQ2=sQuery(id+"F19.wireOp",EDGE,"E117");Q4=makeQuery(id+"F20.opExtrude","SWEPT_EDGE",EDGE,{"disambiguationData":[OSD([subQ0,subQ1,subQ2]),TDD([makeQuery(id+"F19.imprint","INTERSECT",VERTEX,{"disambiguationData":[OD(1.0)],"derivedFrom":[makeQuery(id+"F18.opPattern","COPY",EDGE,{"derivedFrom":makeQuery(id+"F17.opPattern","COPY",EDGE,{"derivedFrom":makeQuery(id+"F16.opExtrude","CAP_EDGE",EDGE,{"disambiguationData":[OSD([subQ0])],"isStart":false}),"instanceName":"1"}),"instanceName":"1"}),subQ1,subQ2]})]),ownerDisambiguation([makeQuery(id+"F20.opExtrude","SWEPT_BODY",BODY,{"disambiguationData":[OSD([subQ0,sQuery(id+"F19.wireOp",EDGE,"E104"),sQuery(id+"F19.wireOp",EDGE,"E105"),sQuery(id+"F19.wireOp",EDGE,"E106.MirrorCS"),sQuery(id+"F19.wireOp",EDGE,"E107.MirrorCS"),sQuery(id+"F19.wireOp",EDGE,"E108"),subQ1,sQuery(id+"F19.wireOp",EDGE,"E111"),sQuery(id+"F19.wireOp",EDGE,"E112"),sQuery(id+"F19.wireOp",EDGE,"E114.MirrorCS"),sQuery(id+"F19.wireOp",EDGE,"E115.MirrorCS")])]})])]});}
            var Q5;
            Q5=makeQuery(id+"F20.opExtrude","SWEPT_EDGE",EDGE,{"disambiguationData":[OSD([sQuery(id+"F19.wireOp",EDGE,"E114.MirrorCS"),sQuery(id+"F19.wireOp",EDGE,"E115.MirrorCS")])]});
            var Q6;
            Q6=makeQuery(id+"F20.opExtrude","SWEPT_EDGE",EDGE,{"disambiguationData":[OSD([sQuery(id+"F15.wireOp",EDGE,"E80"),sQuery(id+"F19.wireOp",EDGE,"E114.MirrorCS"),sQuery(id+"F19.wireOp",EDGE,"E116.MirrorCS")])]});
            var Q7;
            Q7=makeQuery(id+"F20.opExtrude","SWEPT_EDGE",EDGE,{"disambiguationData":[OSD([sQuery(id+"F15.wireOp",EDGE,"E80"),sQuery(id+"F19.wireOp",EDGE,"E115.MirrorCS"),sQuery(id+"F19.wireOp",EDGE,"E116.MirrorCS")])]});
            fillet(context, id + "F21", {"entities" : qUnion([Q0, Q1, Q2, Q3, Q4, Q5, Q6, Q7]), "radius" : 5.08 * mm, "tangentPropagation" : true, "allowEdgeOverflow" : false});
        }
        {
            var Q0;
            Q0=makeQuery(id+"F18.opPattern","COPY",BODY,{"derivedFrom":makeQuery(id+"F17.opPattern","COPY",BODY,{"derivedFrom":makeQuery(id+"F16.opExtrude","SWEPT_BODY",BODY,{"disambiguationData":[OSD([sQuery(id+"F15.wireOp",EDGE,"E69"),sQuery(id+"F15.wireOp",EDGE,"E70"),sQuery(id+"F15.wireOp",EDGE,"E71"),sQuery(id+"F15.wireOp",EDGE,"E72"),sQuery(id+"F15.wireOp",EDGE,"E73"),sQuery(id+"F15.wireOp",EDGE,"E74"),sQuery(id+"F15.wireOp",EDGE,"E75"),sQuery(id+"F15.wireOp",EDGE,"E76"),sQuery(id+"F15.wireOp",EDGE,"E77.MirrorCS"),sQuery(id+"F15.wireOp",EDGE,"E78.MirrorCS"),sQuery(id+"F15.wireOp",EDGE,"E79.MirrorCS"),sQuery(id+"F15.wireOp",EDGE,"E80"),sQuery(id+"F15.wireOp",EDGE,"E81.filletArc"),sQuery(id+"F15.wireOp",EDGE,"E82.filletArc"),sQuery(id+"F15.wireOp",EDGE,"E83.filletArc"),sQuery(id+"F15.wireOp",EDGE,"E84.filletArc"),sQuery(id+"F15.wireOp",EDGE,"E85.filletArc"),sQuery(id+"F15.wireOp",EDGE,"E86.filletArc"),sQuery(id+"F15.wireOp",EDGE,"E87.filletArc"),sQuery(id+"F15.wireOp",EDGE,"E88.filletArc"),sQuery(id+"F15.wireOp",EDGE,"E89"),sQuery(id+"F15.wireOp",EDGE,"E90"),sQuery(id+"F15.wireOp",EDGE,"E91"),sQuery(id+"F15.wireOp",EDGE,"E92.filletArc"),sQuery(id+"F15.wireOp",EDGE,"E93.filletArc"),sQuery(id+"F15.wireOp",EDGE,"E94.filletArc"),sQuery(id+"F15.wireOp",EDGE,"E95.MirrorCS"),sQuery(id+"F15.wireOp",EDGE,"E96.MirrorCS"),sQuery(id+"F15.wireOp",EDGE,"E97.MirrorCS"),sQuery(id+"F15.wireOp",EDGE,"E98.MirrorCS"),sQuery(id+"F15.wireOp",EDGE,"E99.MirrorCS"),sQuery(id+"F15.wireOp",EDGE,"E100.MirrorCS"),sQuery(id+"F15.wireOp",EDGE,"E101"),sQuery(id+"F15.wireOp",EDGE,"E102")])]}),"instanceName":"1"}),"instanceName":"1"});
            var Q1;
            Q1=qCreatedBy(makeId("Right.planeOp"),FACE);
            mirror(context, id + "F22", {"entities" : qUnion([Q0]), "mirrorPlane" : qUnion([Q1])});
        }
        {
            var Q0;
            {var subQ0=sQuery(id+"F15.wireOp",EDGE,"E80");Q0=makeQuery(id+"F22.opPattern","COPY",FACE,{"derivedFrom":makeQuery(id+"F20.boolean.opBoolean","MERGE",FACE,{"derivedFrom":[makeQuery(id+"F18.opPattern","COPY",FACE,{"derivedFrom":makeQuery(id+"F17.opPattern","COPY",FACE,{"derivedFrom":makeQuery(id+"F16.opExtrude","CAP_FACE",FACE,{"disambiguationData":[OSD([sQuery(id+"F15.wireOp",EDGE,"E69"),sQuery(id+"F15.wireOp",EDGE,"E70"),sQuery(id+"F15.wireOp",EDGE,"E71"),sQuery(id+"F15.wireOp",EDGE,"E72"),sQuery(id+"F15.wireOp",EDGE,"E73"),sQuery(id+"F15.wireOp",EDGE,"E74"),sQuery(id+"F15.wireOp",EDGE,"E75"),sQuery(id+"F15.wireOp",EDGE,"E76"),sQuery(id+"F15.wireOp",EDGE,"E77.MirrorCS"),sQuery(id+"F15.wireOp",EDGE,"E78.MirrorCS"),sQuery(id+"F15.wireOp",EDGE,"E79.MirrorCS"),subQ0,sQuery(id+"F15.wireOp",EDGE,"E81.filletArc"),sQuery(id+"F15.wireOp",EDGE,"E82.filletArc"),sQuery(id+"F15.wireOp",EDGE,"E83.filletArc"),sQuery(id+"F15.wireOp",EDGE,"E84.filletArc"),sQuery(id+"F15.wireOp",EDGE,"E85.filletArc"),sQuery(id+"F15.wireOp",EDGE,"E86.filletArc"),sQuery(id+"F15.wireOp",EDGE,"E87.filletArc"),sQuery(id+"F15.wireOp",EDGE,"E88.filletArc"),sQuery(id+"F15.wireOp",EDGE,"E89"),sQuery(id+"F15.wireOp",EDGE,"E90"),sQuery(id+"F15.wireOp",EDGE,"E91"),sQuery(id+"F15.wireOp",EDGE,"E92.filletArc"),sQuery(id+"F15.wireOp",EDGE,"E93.filletArc"),sQuery(id+"F15.wireOp",EDGE,"E94.filletArc"),sQuery(id+"F15.wireOp",EDGE,"E95.MirrorCS"),sQuery(id+"F15.wireOp",EDGE,"E96.MirrorCS"),sQuery(id+"F15.wireOp",EDGE,"E97.MirrorCS"),sQuery(id+"F15.wireOp",EDGE,"E98.MirrorCS"),sQuery(id+"F15.wireOp",EDGE,"E99.MirrorCS"),sQuery(id+"F15.wireOp",EDGE,"E100.MirrorCS"),sQuery(id+"F15.wireOp",EDGE,"E101"),sQuery(id+"F15.wireOp",EDGE,"E102")])],"isStart":false}),"instanceName":"1"}),"instanceName":"1"}),makeQuery(id+"F20.opExtrude","CAP_FACE",FACE,{"disambiguationData":[OSD([subQ0,sQuery(id+"F19.wireOp",EDGE,"E104"),sQuery(id+"F19.wireOp",EDGE,"E105"),sQuery(id+"F19.wireOp",EDGE,"E106.MirrorCS"),sQuery(id+"F19.wireOp",EDGE,"E107.MirrorCS"),sQuery(id+"F19.wireOp",EDGE,"E108"),sQuery(id+"F19.wireOp",EDGE,"E110"),sQuery(id+"F19.wireOp",EDGE,"E111"),sQuery(id+"F19.wireOp",EDGE,"E112"),sQuery(id+"F19.wireOp",EDGE,"E114.MirrorCS"),sQuery(id+"F19.wireOp",EDGE,"E115.MirrorCS")])],"isStart":true})]}),"instanceName":"1"});}
            var sketch = newSketch(context, id + "F23", { "sketchPlane" : qUnion([Q0])});
            skCircle(sketch, "E118", {"center": v(0, 109.81) * mm, "radius": 53.98 * mm});
            skCircle(sketch, "E119", {"center": v(0, 109.81) * mm, "radius": 63.5 * mm});
            skSolve(sketch);
        }
        {
            var Q0;
            Q0 = qSketchRegion(id + "F23", true);
            extrude(context, id + "F24", {"entities" : qUnion([Q0]), "depth" : 19.05 * mm});
        }
        {
            var Q0;
            Q0=makeQuery(id+"F24.opExtrude","SWEPT_BODY",BODY,{"disambiguationData":[OSD([sQuery(id+"F23.wireOp",EDGE,"E118"),sQuery(id+"F23.wireOp",EDGE,"E119")])]});
            var Q1;
            Q1=qCreatedBy(makeId("Right.planeOp"),FACE);
            mirror(context, id + "F25", {"entities" : qUnion([Q0]), "mirrorPlane" : qUnion([Q1])});
        }
        {
            var Q0;
            Q0 = qSketchRegion(id + "F7", true);
            var Q1;
            Q1=sQuery(id+"F7.wireOp",EDGE,"E19");
            var Q2;
            Q2=sQuery(id+"F7.wireOp",EDGE,"E18");
            revolve(context, id + "F26", {"bodyType" : ExtendedToolBodyType.SURFACE, "entities" : qUnion([Q0]), "surfaceEntities" : qUnion([Q1]), "axis" : qUnion([Q2]), "revolveType" : RevolveType.FULL});
        }
        {
            var Q0;
            Q0=makeQuery(id+"F26.opRevolve","SWEPT_FACE",FACE,{"disambiguationData":[OSD([sQuery(id+"F7.wireOp",EDGE,"E19")])]});
            var sketch = newSketch(context, id + "F27", { "sketchPlane" : qUnion([Q0])});
            skCircle(sketch, "E120", {"center": v(0, 0) * mm, "radius": 104.14 * mm});
            skLineSegment(sketch, "E121", {"start": v(-25.4, 129.5) * mm, "end": v(25.4, 129.5) * mm});
            skLineSegment(sketch, "E122", {"start": v(25.4, 129.5) * mm, "end": v(63.28, 107.12) * mm});
            skLineSegment(sketch, "E123", {"start": v(-25.4, 129.5) * mm, "end": v(-63.28, 107.12) * mm});
            skLineSegment(sketch, "E124", {"start": v(-107.12, 63.28) * mm, "end": v(-129.5, 25.4) * mm});
            skLineSegment(sketch, "E125", {"start": v(-129.5, 25.4) * mm, "end": v(-129.5, -25.4) * mm});
            skLineSegment(sketch, "E126", {"start": v(-129.5, -25.4) * mm, "end": v(-107.12, -63.28) * mm});
            skArc(sketch, "E127", {"start": v(-63.28, 107.12) * mm, "mid": v(-87.98, 87.98) * mm, "end": v(-107.12, 63.28) * mm});
            skArc(sketch, "E128.MirrorCS", {"start": v(63.28, 107.12) * mm, "mid": v(87.98, 87.98) * mm, "end": v(107.12, 63.28) * mm});
            skLineSegment(sketch, "E129.MirrorCS", {"start": v(107.12, 63.28) * mm, "end": v(129.5, 25.4) * mm});
            skLineSegment(sketch, "E130.MirrorCS", {"start": v(129.5, 25.4) * mm, "end": v(129.5, -25.4) * mm});
            skLineSegment(sketch, "E131.MirrorCS", {"start": v(129.5, -25.4) * mm, "end": v(107.12, -63.28) * mm});
            skArc(sketch, "E132.MirrorCS", {"start": v(-63.28, -107.12) * mm, "mid": v(-87.98, -87.98) * mm, "end": v(-107.12, -63.28) * mm});
            skLineSegment(sketch, "E133.MirrorCS", {"start": v(-25.4, -129.5) * mm, "end": v(-63.28, -107.12) * mm});
            skLineSegment(sketch, "E134.MirrorCS", {"start": v(-25.4, -129.5) * mm, "end": v(25.4, -129.5) * mm});
            skLineSegment(sketch, "E135.MirrorCS", {"start": v(25.4, -129.5) * mm, "end": v(63.28, -107.12) * mm});
            skArc(sketch, "E136.MirrorCS", {"start": v(63.28, -107.12) * mm, "mid": v(87.98, -87.98) * mm, "end": v(107.12, -63.28) * mm});
            skSolve(sketch);
        }
        {
            var Q0;
            Q0=makeQuery(id+"F27.imprint","IMPRINT",FACE,{"disambiguationData":[TD([[makeQuery(id+"F27.imprint","IMPRINT",EDGE,{"derivedFrom":sQuery(id+"F27.wireOp",EDGE,"E120")}),-1.0]])]});
            extrude(context, id + "F28", {"entities" : qUnion([Q0]), "depth" : 9.52 * mm});
        }
        {
            var Q0;
            Q0=makeQuery(id+"F28.opExtrude","SWEPT_FACE",FACE,{"disambiguationData":[OSD([sQuery(id+"F27.wireOp",EDGE,"E134.MirrorCS")])]});
            var sketch = newSketch(context, id + "F29", { "sketchPlane" : qUnion([Q0])});
            skLineSegment(sketch, "E137", {"start": v(-25.4, 756) * mm, "end": v(25.4, 756) * mm});
            skLineSegment(sketch, "E138", {"start": v(25.4, 756) * mm, "end": v(25.4, 736.32) * mm});
            skLineSegment(sketch, "E139", {"start": v(12.95, 723.88) * mm, "end": v(-12.95, 723.88) * mm});
            skLineSegment(sketch, "E140", {"start": v(-25.4, 736.32) * mm, "end": v(-25.4, 756) * mm});
            skPoint(sketch, "E141.visualSharp", {"position": v(25.4, 723.88) * mm});
            skArc(sketch, "E141.filletArc", {"start": v(12.95, 723.88) * mm, "mid": v(21.75, 727.52) * mm, "end": v(25.4, 736.32) * mm});
            skPoint(sketch, "E142.visualSharp", {"position": v(-25.4, 723.88) * mm});
            skArc(sketch, "E142.filletArc", {"start": v(-25.4, 736.32) * mm, "mid": v(-21.75, 727.52) * mm, "end": v(-12.95, 723.88) * mm});
            skCircle(sketch, "E143", {"center": v(12.95, 736.32) * mm, "radius": 1.27 * mm});
            skCircle(sketch, "E144", {"center": v(-12.95, 736.32) * mm, "radius": 1.27 * mm});
            skSolve(sketch);
        }
        {
            var Q0;
            Q0 = qSketchRegion(id + "F29", true);
            extrude(context, id + "F30", {"entities" : qUnion([Q0]), "depth" : 9.52 * mm});
        }
        {
            var Q0;
            Q0=makeQuery(id+"F30.opExtrude","SWEPT_BODY",BODY,{"disambiguationData":[OSD([sQuery(id+"F29.wireOp",EDGE,"E137"),sQuery(id+"F29.wireOp",EDGE,"E138"),sQuery(id+"F29.wireOp",EDGE,"E139"),sQuery(id+"F29.wireOp",EDGE,"E140"),sQuery(id+"F29.wireOp",EDGE,"E141.filletArc"),sQuery(id+"F29.wireOp",EDGE,"E142.filletArc"),sQuery(id+"F29.wireOp",EDGE,"E143"),sQuery(id+"F29.wireOp",EDGE,"E144")])]});
            var Q1;
            Q1=sQuery(id+"F7.wireOp",EDGE,"E18");
            circularPattern(context, id + "F31", {"entities" : qUnion([Q0]), "axis" : qUnion([Q1]), "angle" : 90 * degree, "instanceCount" : 4, "computeTransformsWithoutBuiltin" : true});
        }
    });
